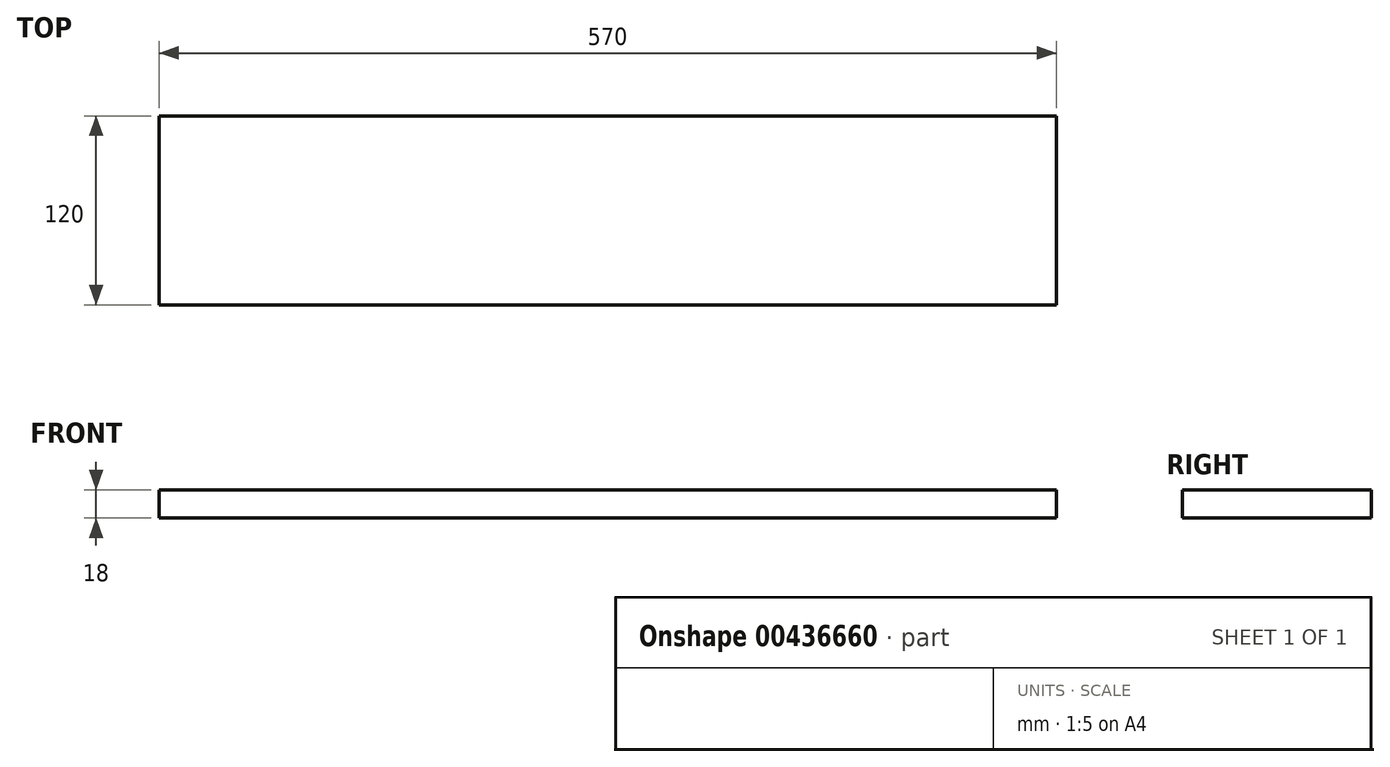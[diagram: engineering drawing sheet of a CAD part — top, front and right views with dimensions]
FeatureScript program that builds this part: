
annotation { "Feature Type Name" : "Feature", "Feature Type Description" : "" }
export const myFeature = defineFeature(function(context is Context, id is Id, definition is map)
    precondition{}
    {
        {
            var Q0;
            Q0=qCreatedBy(makeId("Right.planeOp"),FACE);
            var sketch = newSketch(context, id + "F0", { "sketchPlane" : qUnion([Q0])});
            skLineSegment(sketch, "E0.bottom", {"start": v(60, -9) * mm, "end": v(-60, -9) * mm});
            skLineSegment(sketch, "E0.top", {"start": v(60, 9) * mm, "end": v(-60, 9) * mm});
            skLineSegment(sketch, "E0.left", {"start": v(60, -9) * mm, "end": v(60, 9) * mm});
            skLineSegment(sketch, "E0.right", {"start": v(-60, -9) * mm, "end": v(-60, 9) * mm});
            skPoint(sketch, "E0.middle", {"position": v(0, 0) * mm});
            skSolve(sketch);
        }
        {
            var Q0;
            Q0 = qSketchRegion(id + "F0", true);
            extrude(context, id + "F1", {"entities" : qUnion([Q0]), "depth" : 570 * mm});
        }
    });
